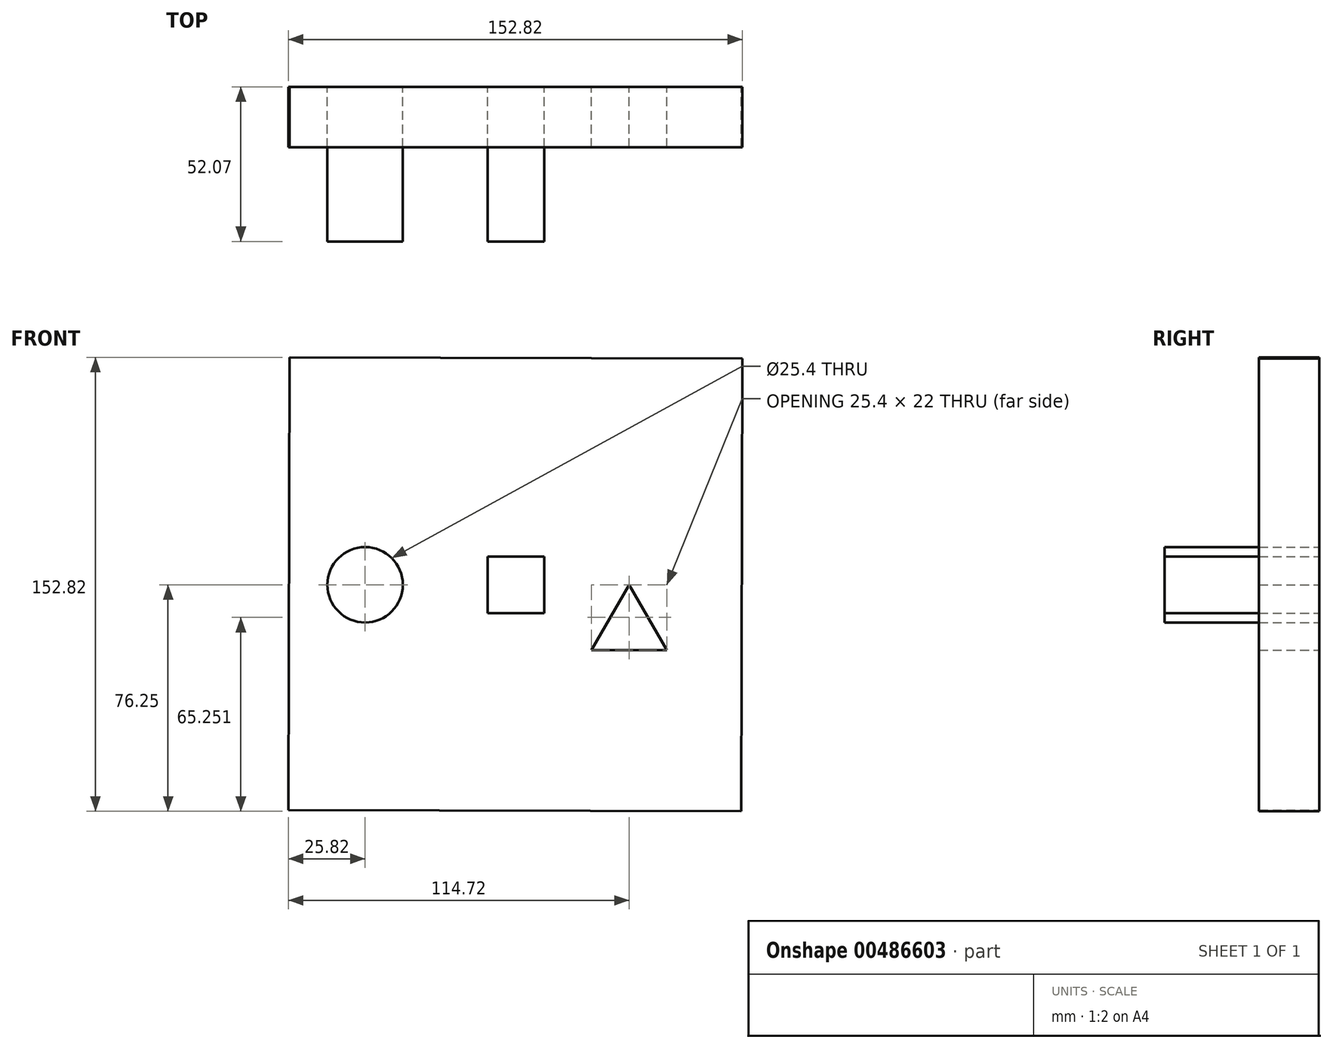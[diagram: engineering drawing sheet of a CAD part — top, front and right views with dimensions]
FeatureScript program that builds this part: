
annotation { "Feature Type Name" : "Feature", "Feature Type Description" : "" }
export const myFeature = defineFeature(function(context is Context, id is Id, definition is map)
    precondition{}
    {
        {
            var Q0;
            Q0=qCreatedBy(makeId("Front.planeOp"),FACE);
            var sketch = newSketch(context, id + "F0", { "sketchPlane" : qUnion([Q0])});
            skPoint(sketch, "E0", {"position": v(44.45, 0) * mm});
            skLineSegment(sketch, "E1", {"start": v(44.03, -76.25) * mm, "end": v(44.45, 76.15) * mm});
            skLineSegment(sketch, "E2", {"start": v(44.45, 76.15) * mm, "end": v(-107.95, 76.57) * mm});
            skLineSegment(sketch, "E3", {"start": v(44.03, -76.25) * mm, "end": v(-108.37, -75.83) * mm});
            skLineSegment(sketch, "E4", {"start": v(-107.95, 76.57) * mm, "end": v(-108.37, -75.83) * mm});
            skPoint(sketch, "E5", {"position": v(6.35, 0) * mm});
            skLineSegment(sketch, "E6", {"start": v(6.35, 0) * mm, "end": v(-6.35, -22) * mm});
            skLineSegment(sketch, "E7", {"start": v(-6.35, -22) * mm, "end": v(19.05, -22) * mm});
            skLineSegment(sketch, "E8", {"start": v(19.05, -22) * mm, "end": v(6.35, 0) * mm});
            skLineSegment(sketch, "E9.bottom", {"start": v(-41.27, -9.52) * mm, "end": v(-22.22, -9.52) * mm});
            skLineSegment(sketch, "E9.top", {"start": v(-41.27, 9.52) * mm, "end": v(-22.22, 9.52) * mm});
            skLineSegment(sketch, "E9.left", {"start": v(-41.27, -9.52) * mm, "end": v(-41.27, 9.52) * mm});
            skLineSegment(sketch, "E9.right", {"start": v(-22.22, -9.52) * mm, "end": v(-22.22, 9.53) * mm});
            skPoint(sketch, "E9.middle", {"position": v(-31.75, 0) * mm});
            skCircle(sketch, "E10", {"center": v(-82.55, 0) * mm, "radius": 12.7 * mm});
            skSolve(sketch);
        }
        {
            var Q0;
            Q0 = qSketchRegion(id + "F0", true);
            extrude(context, id + "F1", {"entities" : qUnion([Q0]), "depth" : 20.32 * mm});
        }
        {
            var Q0;
            Q0=makeQuery(id+"F0.imprint","IMPRINT",FACE,{"disambiguationData":[TD([[makeQuery(id+"F0.imprint","IMPRINT",EDGE,{"derivedFrom":sQuery(id+"F0.wireOp",EDGE,"E10")}),1.0]])]});
            var Q1;
            Q1=makeQuery(id+"F0.imprint","IMPRINT",FACE,{"disambiguationData":[TD([[makeQuery(id+"F0.imprint","IMPRINT",EDGE,{"derivedFrom":sQuery(id+"F0.wireOp",EDGE,"E9.bottom")}),1.0]])]});
            extrude(context, id + "F2", {"entities" : qUnion([Q0, Q1]), "depth" : 52.07 * mm});
        }
    });
